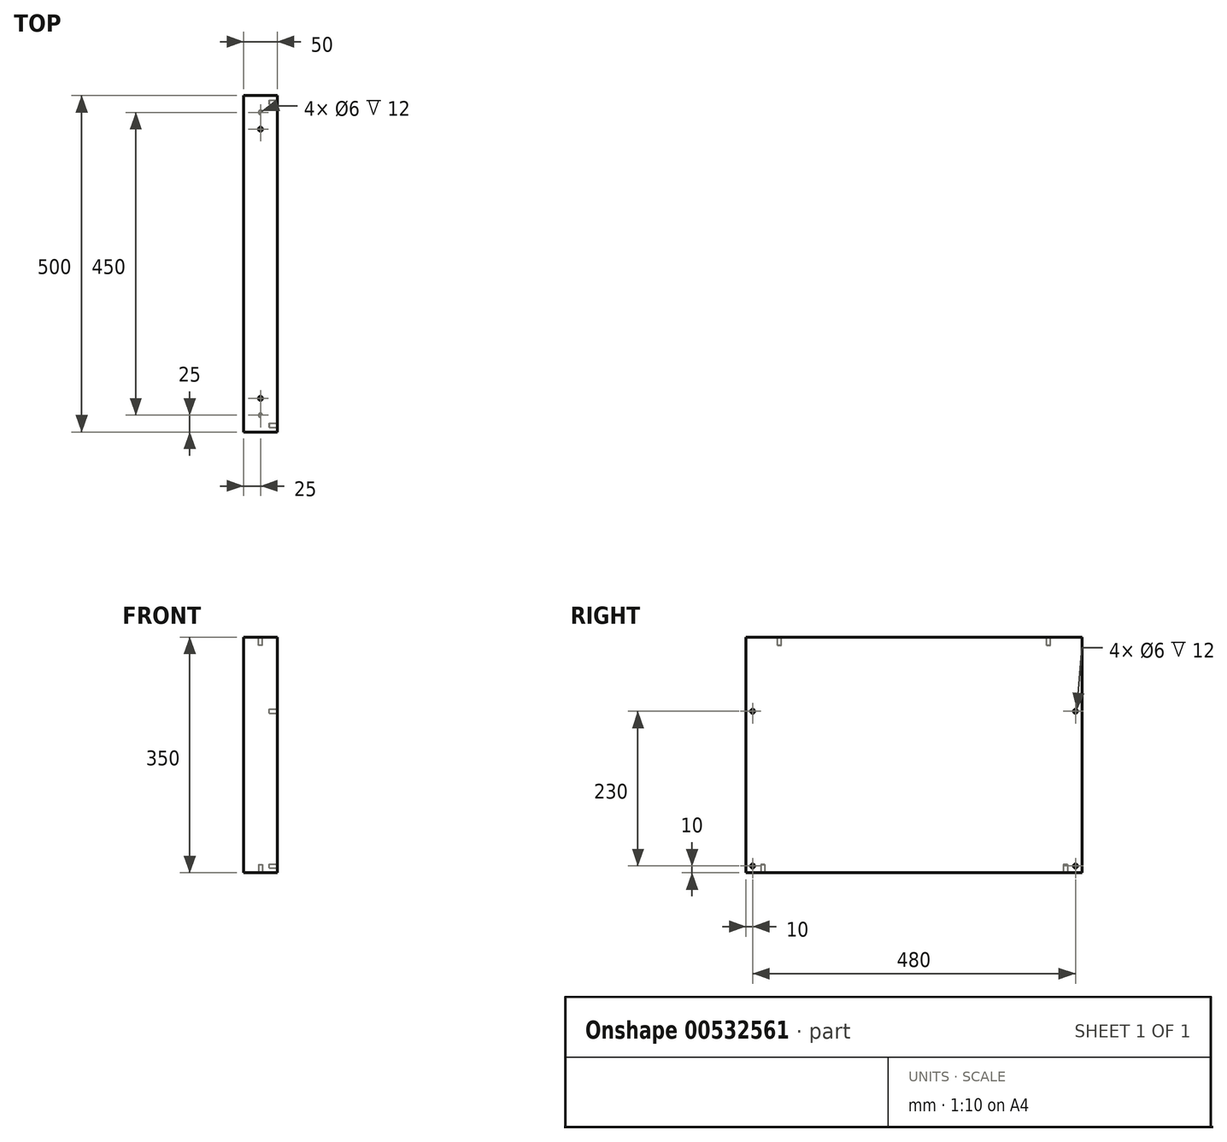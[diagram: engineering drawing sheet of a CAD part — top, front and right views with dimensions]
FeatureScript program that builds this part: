
annotation { "Feature Type Name" : "Feature", "Feature Type Description" : "" }
export const myFeature = defineFeature(function(context is Context, id is Id, definition is map)
    precondition{}
    {
        {
            var Q0;
            Q0=qCreatedBy(makeId("Right.planeOp"),FACE);
            var sketch = newSketch(context, id + "F0", { "sketchPlane" : qUnion([Q0])});
            skLineSegment(sketch, "E0.bottom", {"start": v(0, 0) * mm, "end": v(500, 0) * mm});
            skLineSegment(sketch, "E0.top", {"start": v(0, 350) * mm, "end": v(500, 350) * mm});
            skLineSegment(sketch, "E0.left", {"start": v(0, 0) * mm, "end": v(0, 350) * mm});
            skLineSegment(sketch, "E0.right", {"start": v(500, 0) * mm, "end": v(500, 350) * mm});
            skSolve(sketch);
        }
        {
            var Q0;
            Q0 = qSketchRegion(id + "F0", true);
            extrude(context, id + "F1", {"entities" : qUnion([Q0]), "depth" : 50 * mm, "offsetDistance" : 25 * mm});
        }
        {
            var Q0;
            Q0=makeQuery(id+"F1.opExtrude","SWEPT_FACE",FACE,{"disambiguationData":[OSD([sQuery(id+"F0.wireOp",EDGE,"E0.top")])]});
            var sketch = newSketch(context, id + "F2", { "sketchPlane" : qUnion([Q0])});
            skCircle(sketch, "E1", {"center": v(25, 50) * mm, "radius": 3 * mm});
            skCircle(sketch, "E2", {"center": v(25, 450) * mm, "radius": 3 * mm});
            skSolve(sketch);
        }
        {
            var Q0;
            Q0=makeQuery(id+"F2.imprint","IMPRINT",FACE,{"disambiguationData":[TD([[makeQuery(id+"F2.imprint","IMPRINT",EDGE,{"derivedFrom":sQuery(id+"F2.wireOp",EDGE,"E1")}),1.0]])]});
            extrude(context, id + "F3", {"entities" : qUnion([Q0]), "operationType" : NewBodyOperationType.REMOVE, "oppositeDirection" : true, "depth" : 12 * mm, "offsetDistance" : 25 * mm});
        }
        {
            var Q0;
            Q0=makeQuery(id+"F2.imprint","IMPRINT",FACE,{"disambiguationData":[TD([[makeQuery(id+"F2.imprint","IMPRINT",EDGE,{"derivedFrom":sQuery(id+"F2.wireOp",EDGE,"E2")}),1.0]])]});
            extrude(context, id + "F4", {"entities" : qUnion([Q0]), "operationType" : NewBodyOperationType.REMOVE, "oppositeDirection" : true, "depth" : 12 * mm, "offsetDistance" : 25 * mm});
        }
        {
            var Q0;
            Q0=makeQuery(id+"F1.opExtrude","CAP_FACE",FACE,{"disambiguationData":[OSD([sQuery(id+"F0.wireOp",EDGE,"E0.bottom"),sQuery(id+"F0.wireOp",EDGE,"E0.top"),sQuery(id+"F0.wireOp",EDGE,"E0.left"),sQuery(id+"F0.wireOp",EDGE,"E0.right")])],"isStart":false});
            var sketch = newSketch(context, id + "F5", { "sketchPlane" : qUnion([Q0])});
            skCircle(sketch, "E3", {"center": v(10, 240) * mm, "radius": 3 * mm});
            skCircle(sketch, "E4", {"center": v(10, 10) * mm, "radius": 3 * mm});
            skSolve(sketch);
        }
        {
            var Q0;
            Q0 = qSketchRegion(id + "F5", true);
            extrude(context, id + "F6", {"entities" : qUnion([Q0]), "operationType" : NewBodyOperationType.REMOVE, "oppositeDirection" : true, "depth" : 12 * mm, "offsetDistance" : 25 * mm});
        }
        {
            var Q0;
            Q0=makeQuery(id+"F1.opExtrude","CAP_FACE",FACE,{"disambiguationData":[OSD([sQuery(id+"F0.wireOp",EDGE,"E0.bottom"),sQuery(id+"F0.wireOp",EDGE,"E0.top"),sQuery(id+"F0.wireOp",EDGE,"E0.left"),sQuery(id+"F0.wireOp",EDGE,"E0.right")])],"isStart":false});
            var sketch = newSketch(context, id + "F7", { "sketchPlane" : qUnion([Q0])});
            skCircle(sketch, "E5", {"center": v(490, 240) * mm, "radius": 3 * mm});
            skCircle(sketch, "E6", {"center": v(490, 10) * mm, "radius": 3 * mm});
            skSolve(sketch);
        }
        {
            var Q0;
            Q0 = qSketchRegion(id + "F7", true);
            extrude(context, id + "F8", {"entities" : qUnion([Q0]), "operationType" : NewBodyOperationType.REMOVE, "oppositeDirection" : true, "depth" : 12 * mm, "offsetDistance" : 25 * mm});
        }
        {
            var Q0;
            Q0=makeQuery(id+"F1.opExtrude","SWEPT_FACE",FACE,{"disambiguationData":[OSD([sQuery(id+"F0.wireOp",EDGE,"E0.bottom")])]});
            var sketch = newSketch(context, id + "F9", { "sketchPlane" : qUnion([Q0])});
            skCircle(sketch, "E7", {"center": v(25, -25) * mm, "radius": 3 * mm});
            skCircle(sketch, "E8", {"center": v(25, -475) * mm, "radius": 3 * mm});
            skSolve(sketch);
        }
        {
            var Q0;
            Q0 = qSketchRegion(id + "F9", true);
            extrude(context, id + "F10", {"entities" : qUnion([Q0]), "operationType" : NewBodyOperationType.REMOVE, "oppositeDirection" : true, "depth" : 12 * mm, "offsetDistance" : 25 * mm});
        }
    });
